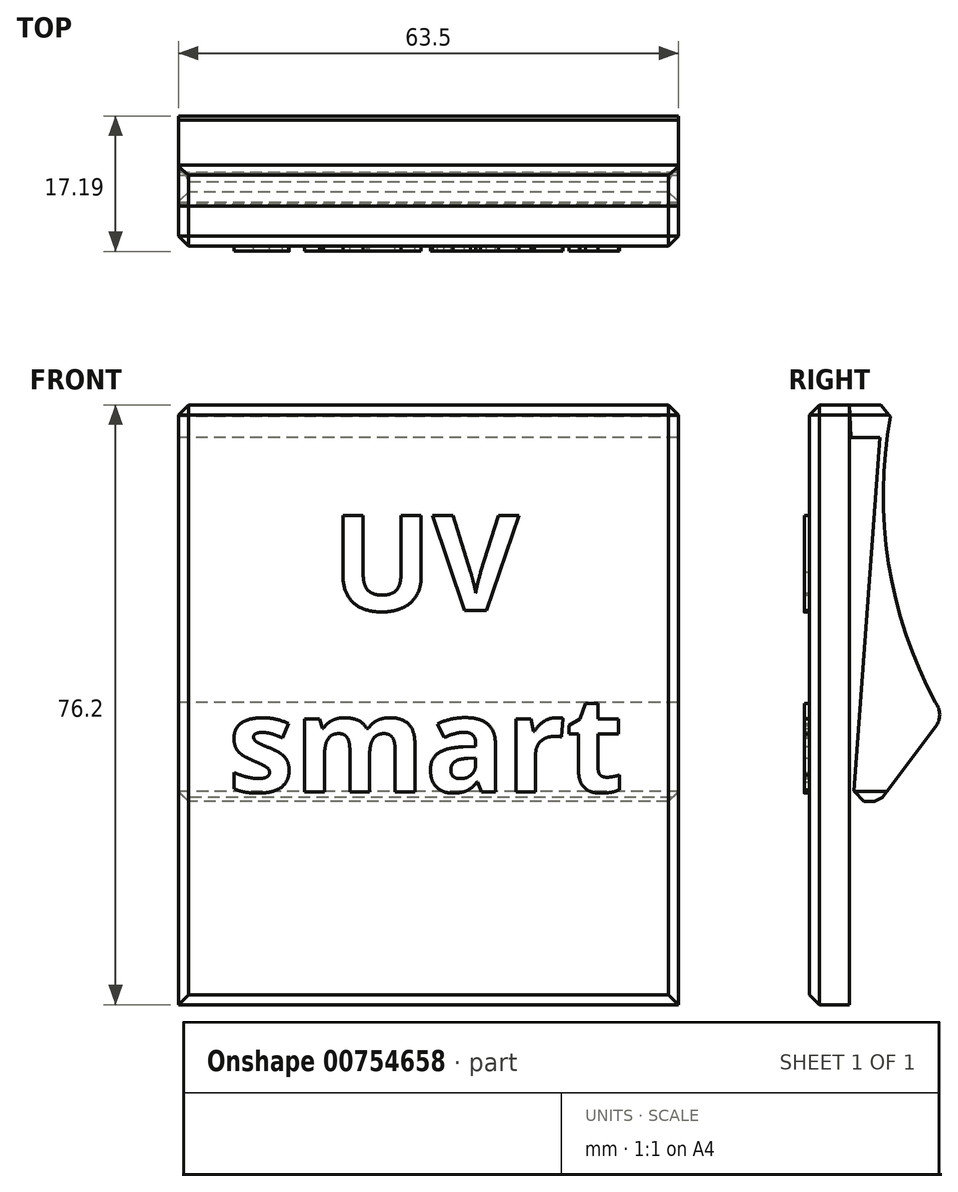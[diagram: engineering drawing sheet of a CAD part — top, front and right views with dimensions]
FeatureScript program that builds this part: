
annotation { "Feature Type Name" : "Feature", "Feature Type Description" : "" }
export const myFeature = defineFeature(function(context is Context, id is Id, definition is map)
    precondition{}
    {
        {
            var Q0;
            Q0=qCreatedBy(makeId("Front.planeOp"),FACE);
            var sketch = newSketch(context, id + "F0", { "sketchPlane" : qUnion([Q0])});
            skLineSegment(sketch, "E0.bottom", {"start": v(31.75, -38.1) * mm, "end": v(-31.75, -38.1) * mm});
            skLineSegment(sketch, "E0.top", {"start": v(31.75, 38.1) * mm, "end": v(-31.75, 38.1) * mm});
            skLineSegment(sketch, "E0.left", {"start": v(31.75, -38.1) * mm, "end": v(31.75, 38.1) * mm});
            skLineSegment(sketch, "E0.right", {"start": v(-31.75, -38.1) * mm, "end": v(-31.75, 38.1) * mm});
            skPoint(sketch, "E0.middle", {"position": v(0, 0) * mm});
            skSolve(sketch);
        }
        {
            var Q0;
            Q0 = qSketchRegion(id + "F0", true);
            extrude(context, id + "F1", {"entities" : qUnion([Q0]), "depth" : 5.08 * mm, "offsetDistance" : 25.4 * mm});
        }
        {
            var Q0;
            Q0=qCreatedBy(makeId("Right.planeOp"),FACE);
            var sketch = newSketch(context, id + "F2", { "sketchPlane" : qUnion([Q0])});
            skLineSegment(sketch, "E1", {"start": v(0, 38.1) * mm, "end": v(5.53, 38.1) * mm});
            skArc(sketch, "E2", {"start": v(5.53, 38.1) * mm, "mid": v(4.85, 18.71) * mm, "end": v(10.95, 0.3) * mm});
            skLineSegment(sketch, "E3", {"start": v(3.9, 33.98) * mm, "end": v(0.21, 33.98) * mm});
            skLineSegment(sketch, "E4", {"start": v(0.21, 33.98) * mm, "end": v(0, 38.1) * mm});
            skLineSegment(sketch, "E5", {"start": v(3.9, 33.98) * mm, "end": v(0.46, -12.3) * mm});
            skLineSegment(sketch, "E6", {"start": v(0.46, -12.3) * mm, "end": v(3.8, -12.3) * mm});
            skLineSegment(sketch, "E7", {"start": v(3.8, -12.3) * mm, "end": v(10.95, -2.81) * mm});
            skArc(sketch, "E8", {"start": v(10.95, -2.81) * mm, "mid": v(11.47, -1.26) * mm, "end": v(10.95, 0.3) * mm});
            skSolve(sketch);
        }
        {
            var Q0;
            Q0 = qSketchRegion(id + "F2", true);
            extrude(context, id + "F3", {"entities" : qUnion([Q0]), "depth" : 31.75 * mm, "offsetDistance" : 25.4 * mm, "hasSecondDirection" : true, "secondDirectionOppositeDirection" : true, "secondDirectionDepth" : 31.75 * mm});
        }
        {
            var Q0;
            Q0=makeQuery(id+"F1.opExtrude","CAP_EDGE",EDGE,{"disambiguationData":[OSD([sQuery(id+"F0.wireOp",EDGE,"E0.top")])],"isStart":false});
            var Q1;
            Q1=makeQuery(id+"F1.opExtrude","CAP_EDGE",EDGE,{"disambiguationData":[OSD([sQuery(id+"F0.wireOp",EDGE,"E0.left")])],"isStart":false});
            var Q2;
            Q2=makeQuery(id+"F1.opExtrude","CAP_EDGE",EDGE,{"disambiguationData":[OSD([sQuery(id+"F0.wireOp",EDGE,"E0.bottom")])],"isStart":false});
            var Q3;
            Q3=makeQuery(id+"F1.opExtrude","CAP_EDGE",EDGE,{"disambiguationData":[OSD([sQuery(id+"F0.wireOp",EDGE,"E0.right")])],"isStart":false});
            var Q4;
            Q4=makeQuery(id+"F3.opExtrude","SWEPT_EDGE",EDGE,{"disambiguationData":[OSD([sQuery(id+"F2.wireOp",EDGE,"E1"),sQuery(id+"F2.wireOp",EDGE,"E2")])]});
            var Q5;
            Q5=makeQuery(id+"F3.opExtrude","CAP_EDGE",EDGE,{"disambiguationData":[OSD([sQuery(id+"F2.wireOp",EDGE,"E6")])],"isStart":false});
            var Q6;
            Q6=makeQuery(id+"F3.opExtrude","SWEPT_EDGE",EDGE,{"disambiguationData":[OSD([sQuery(id+"F2.wireOp",EDGE,"E6"),sQuery(id+"F2.wireOp",EDGE,"RU8pMT6a-zutz-WX36-iFVL-0Q0FUx9y6cPr")])]});
            var Q7;
            Q7=makeQuery(id+"F3.opExtrude","CAP_EDGE",EDGE,{"disambiguationData":[OSD([sQuery(id+"F2.wireOp",EDGE,"E6")])],"isStart":true});
            var Q8;
            Q8=makeQuery(id+"F1.opExtrude","SWEPT_EDGE",EDGE,{"disambiguationData":[OSD([sQuery(id+"F0.wireOp",EDGE,"E0.top"),sQuery(id+"F0.wireOp",EDGE,"E0.left")])]});
            var Q9;
            Q9=makeQuery(id+"F3.opExtrude","CAP_EDGE",EDGE,{"disambiguationData":[OSD([sQuery(id+"F2.wireOp",EDGE,"E1")])],"isStart":false});
            var Q10;
            Q10=makeQuery(id+"F3.opExtrude","CAP_EDGE",EDGE,{"disambiguationData":[OSD([sQuery(id+"F2.wireOp",EDGE,"E1")])],"isStart":true});
            var Q11;
            Q11=makeQuery(id+"F1.opExtrude","SWEPT_EDGE",EDGE,{"disambiguationData":[OSD([sQuery(id+"F0.wireOp",EDGE,"E0.top"),sQuery(id+"F0.wireOp",EDGE,"E0.right")])]});
            chamfer(context, id + "F4", {"entities" : qUnion([Q0, Q1, Q2, Q3, Q4, Q5, Q6, Q7, Q8, Q9, Q10, Q11]), "width" : 1.27 * mm, "tangentPropagation" : true});
        }
        {
            var Q0;
            Q0=makeQuery(id+"F1.opExtrude","CAP_FACE",FACE,{"disambiguationData":[OSD([sQuery(id+"F0.wireOp",EDGE,"E0.bottom"),sQuery(id+"F0.wireOp",EDGE,"E0.top"),sQuery(id+"F0.wireOp",EDGE,"E0.left"),sQuery(id+"F0.wireOp",EDGE,"E0.right")])],"isStart":false});
            var sketch = newSketch(context, id + "F5", { "sketchPlane" : qUnion([Q0])});
            skText(sketch, "E9", { "text": "   UV\nsmart", "fontName": "OpenSans-Bold.ttf"});
            const initialGuessF5  = {"E9": [-0.02547, 0.01195, 1, 0, 0.01218]};
            skSetInitialGuess(sketch, initialGuessF5);
            skSolve(sketch);
        }
        {
            var Q0;
            Q0 = qSketchRegion(id + "F5", true);
            extrude(context, id + "F6", {"entities" : qUnion([Q0]), "operationType" : NewBodyOperationType.ADD, "depth" : 0.64 * mm, "offsetDistance" : 25.4 * mm});
        }
    });
